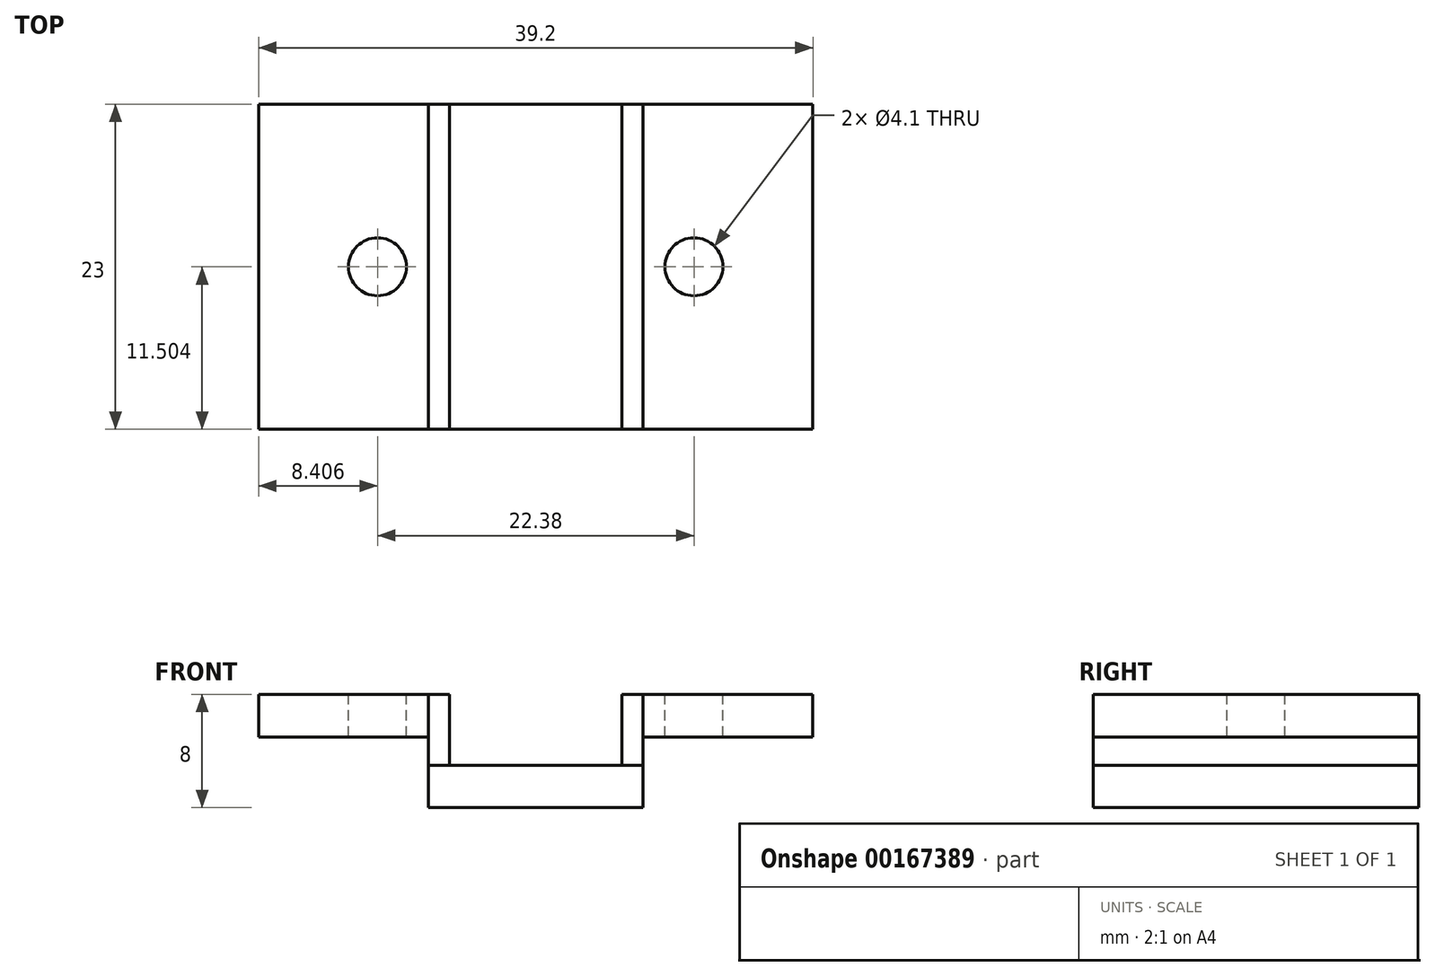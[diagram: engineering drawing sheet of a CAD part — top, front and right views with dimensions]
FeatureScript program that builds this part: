
annotation { "Feature Type Name" : "Feature", "Feature Type Description" : "" }
export const myFeature = defineFeature(function(context is Context, id is Id, definition is map)
    precondition{}
    {
        {
            var Q0;
            Q0=qCreatedBy(makeId("Top.planeOp"),FACE);
            var sketch = newSketch(context, id + "F0", { "sketchPlane" : qUnion([Q0])});
            skLineSegment(sketch, "E0", {"start": v(-5.27, -43.09) * mm, "end": v(6.93, -43.09) * mm});
            skLineSegment(sketch, "E1", {"start": v(6.93, -43.09) * mm, "end": v(6.93, -20.09) * mm});
            skLineSegment(sketch, "E2", {"start": v(-5.27, -43.09) * mm, "end": v(-5.27, -20.09) * mm});
            skLineSegment(sketch, "E3", {"start": v(-5.27, -20.09) * mm, "end": v(6.93, -20.09) * mm});
            skLineSegment(sketch, "E4", {"start": v(6.93, -20.09) * mm, "end": v(20.43, -20.09) * mm});
            skLineSegment(sketch, "E5", {"start": v(20.43, -20.09) * mm, "end": v(20.43, -43.09) * mm});
            skLineSegment(sketch, "E6", {"start": v(20.43, -43.09) * mm, "end": v(6.93, -43.09) * mm});
            skLineSegment(sketch, "E7", {"start": v(-5.27, -20.09) * mm, "end": v(-18.77, -20.09) * mm});
            skLineSegment(sketch, "E8", {"start": v(-18.77, -20.09) * mm, "end": v(-18.77, -43.09) * mm});
            skLineSegment(sketch, "E9", {"start": v(-18.77, -43.09) * mm, "end": v(-5.27, -43.09) * mm});
            skCircle(sketch, "E10.MirrorC", {"center": v(12.02, -31.59) * mm, "radius": 2.05 * mm});
            skLineSegment(sketch, "E11.0", {"start": v(8.43, -43.09) * mm, "end": v(8.43, -20.09) * mm});
            skLineSegment(sketch, "E12.0", {"start": v(-6.77, -43.09) * mm, "end": v(-6.77, -20.09) * mm});
            skCircle(sketch, "E13.MirrorC", {"center": v(-10.36, -31.59) * mm, "radius": 2.05 * mm});
            skSolve(sketch);
        }
        {
            var Q0;
            {var subQ0=sQuery(id+"F0.wireOp",EDGE,"E2");Q0=makeQuery(id+"F0.imprint","IMPRINT",FACE,{"disambiguationData":[TD([[makeQuery(id+"F0.imprint","IMPRINT",EDGE,{"derivedFrom":subQ0}),1.0]])]});}
            var Q1;
            {var subQ0=sQuery(id+"F0.wireOp",EDGE,"E1");Q1=makeQuery(id+"F0.imprint","IMPRINT",FACE,{"disambiguationData":[TD([[makeQuery(id+"F0.imprint","IMPRINT",EDGE,{"derivedFrom":subQ0}),-1.0]])]});}
            extrude(context, id + "F1", {"entities" : qUnion([Q0, Q1]), "oppositeDirection" : true, "depth" : 5 * mm});
        }
        {
            var Q0;
            {var subQ1=sQuery(id+"F0.wireOp",EDGE,"E8");Q0=makeQuery(id+"F0.imprint","IMPRINT",FACE,{"disambiguationData":[TD([[makeQuery(id+"F0.imprint","IMPRINT",EDGE,{"derivedFrom":subQ1}),1.0]])]});}
            var Q1;
            {var subQ1=sQuery(id+"F0.wireOp",EDGE,"E5");Q1=makeQuery(id+"F0.imprint","IMPRINT",FACE,{"disambiguationData":[TD([[makeQuery(id+"F0.imprint","IMPRINT",EDGE,{"derivedFrom":subQ1}),-1.0]])]});}
            extrude(context, id + "F2", {"entities" : qUnion([Q0, Q1]), "oppositeDirection" : true, "depth" : 3 * mm});
        }
        {
            var Q0;
            Q0=makeQuery(id+"F1.opExtrude","CAP_FACE",FACE,{"disambiguationData":[OSD([sQuery(id+"F0.wireOp",EDGE,"E2"),sQuery(id+"F0.wireOp",EDGE,"E7"),sQuery(id+"F0.wireOp",EDGE,"E9"),sQuery(id+"F0.wireOp",EDGE,"E12.0")])],"isStart":false});
            var sketch = newSketch(context, id + "F3", { "sketchPlane" : qUnion([Q0])});
            skLineSegment(sketch, "E14.bottom", {"start": v(-6.77, 43.09) * mm, "end": v(8.43, 43.09) * mm});
            skLineSegment(sketch, "E14.top", {"start": v(-6.77, 20.09) * mm, "end": v(8.43, 20.09) * mm});
            skLineSegment(sketch, "E14.left", {"start": v(-6.77, 43.09) * mm, "end": v(-6.77, 20.09) * mm});
            skLineSegment(sketch, "E14.right", {"start": v(8.43, 43.09) * mm, "end": v(8.43, 20.09) * mm});
            skSolve(sketch);
        }
        {
            var Q0;
            Q0 = qSketchRegion(id + "F3", true);
            extrude(context, id + "F4", {"entities" : qUnion([Q0]), "depth" : 3 * mm});
        }
    });
